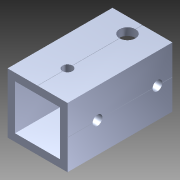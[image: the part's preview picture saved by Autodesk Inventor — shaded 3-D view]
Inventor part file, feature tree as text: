
AUTODESK INVENTOR PART (.ipt)
format: ipt  version: 2014 (Build 180170000, 170)  size: 1,171,968 bytes
history: native  units: in
note: dims shown in document units (in); Inventor stores cm internally (conversion verified against a paired STEP export)
features: extrude x2, sketch x2, pattern_circular x1, other x1, plane x1, imported_body x1
ambient origin geometry x8: Origin, YZ Plane, XZ Plane, XY Plane, X Axis, Y Axis, Z Axis, Center Point
bodies: Body1 (feature_tree)
feature tree (8):
  pattern_circular  "CirPattern2"
  other  "217-3426-STEP1"
  plane  "Work Plane1"
  extrude  "Extrusion1"  Depth=3937.0079in TaperAngle=0.0deg
  extrude  "Extrusion3"  Depth=1.0in TaperAngle=0.0deg
  imported_body  "Base1"
  sketch  "Sketch1"  dims[d0=-1.75in d1=3937.0079in d2=0.0in]
  sketch  "Sketch4"  dims[d6=0.266in d7=1.0in d8=0.0in]
